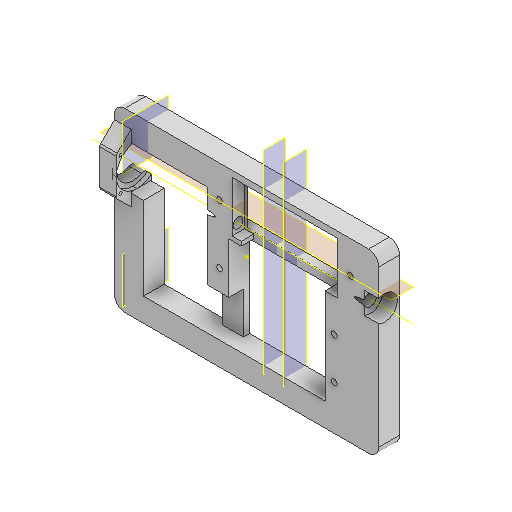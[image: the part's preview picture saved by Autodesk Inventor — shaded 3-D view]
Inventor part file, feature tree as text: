
AUTODESK INVENTOR PART (.ipt)
format: ipt  version: 2022 (Build 260153000, 153)  size: 460,800 bytes
history: native  units: mm
features: sketch x17, extrude x16, other x12, reference x8, plane x7, projected_geometry x7, fillet x3, chamfer x1, mirror x1
ambient origin geometry x8: Origin, YZ Plane, XZ Plane, XY Plane, X Axis, Y Axis, Z Axis, Center Point
bodies: Solid1 (feature_tree)
feature tree (72):
  extrude  "Extrusion1"  Depth=10.0mm
  fillet  "Fillet1"  Radius=10.0mm
  extrude  "Extrusion2"  Depth=51.0mm
  extrude  "Extrusion3"  Depth=20.0mm
  plane  "Work Plane1"
  plane  "Work Plane2"
  chamfer  "Chamfer1"  [1 undecoded]
  plane  "Work Plane3"
  extrude  "Extrusion12"  Depth=10.0mm
  extrude  "Extrusion13"  Depth=12.0mm
  mirror  "Mirror1"
  plane  "Work Plane4"
  plane  "Work Plane5"
  plane  "Arbeitsebene7"
  extrude  "Extrusion27"  Depth=7.0mm
  extrude  "Extrusion28"  Depth=0.5mm TaperAngle=0.0deg
  extrude  "Extrusion29"  Depth=0.5mm
  fillet  "Rundung6"  Radius=1.0mm
  extrude  "Extrusion37"  TaperAngle=45.0deg  [1 undecoded]
  extrude  "Extrusion38"  Depth=10.0mm
  fillet  "Rundung7"  [1 undecoded]
  extrude  "Extrusion39"  Depth=10.0mm TaperAngle=0.0deg
  other  "Arbeitsachse1"
  sketch  "Skizze44"  dims[d145=8.0mm d146=0.0mm d147=0.5mm d148=1.0mm d149=0.0mm]
  extrude  "Extrusion41"  TaperAngle=0.0deg  [1 undecoded]
  extrude  "Extrusion42"  Depth=2.0mm TaperAngle=0.0deg
  extrude  "Extrusion43"  Depth=2.5mm
  extrude  "Extrusion44"  Depth=0.5mm
  sketch  "Skizze49"  dims[d195=20.0mm d196=2.0mm d197=0.0mm d199=14.0mm d201=0.5mm d203=0.5mm d204=1.0mm d205=3.0mm d206=2.8mm d207=2.8mm d208=2.8mm d209=2.8mm d210=2.8mm d211=0.0mm d212=0.0mm d213=3.0mm d214=0.0mm d215=6.0mm d216=2.0mm d217=3.0mm d218=0.0mm d219=2.5mm d220=0.0mm]
  plane  "Arbeitsebene10"
  extrude  "Extrusion45"  Depth=0.5mm
  sketch  "Sketch1"  dims[d0=127.8mm d1=85.5mm d2=10.0mm d3=0.0mm]
  sketch  "Sketch2"  dims[d4=4.0mm d5=51.0mm]
  projected_geometry  "Projected Loop1"
  sketch  "Sketch3"  dims[d6=25.0mm d7=20.0mm]
  projected_geometry  "Projected Loop2"
  sketch  "Sketch12"  dims[d8=13.0mm]
  reference  "Reference4"
  sketch  "Sketch13"  dims[d9=6.0mm]
  sketch  "Skizze28"  dims[d10=0.0mm]
  sketch  "Skizze29"  dims[d11=1.5mm d12=0.0mm d13=0.0mm]
  reference  "Referenz13"
  sketch  "Skizze30"  dims[d14=4.0mm d15=2.0mm d16=45.0deg d38=10.0mm]
  reference  "Referenz14"
  sketch  "Skizze40"  dims[d61=30.0mm d62=-0.523599mm d63=12.0mm]
  projected_geometry  "Projizierte Kontur18"
  sketch  "Skizze41"  dims[d64=7.0mm d65=0.0mm d100=7.0mm]
  projected_geometry  "Projizierte Kontur19"
  sketch  "Skizze42"  dims[d142=0.5mm d143=40.0mm d144=0.0mm]
  reference  "Referenz22"
  reference  "Referenz23"
  reference  "Referenz24"
  reference  "Referenz25"
  sketch  "Skizze45"  dims[d150=2.0mm d151=45.0deg]
  sketch  "Skizze46"  dims[d152=45.0deg d178=10.0mm d179=0.0mm d180=0.0mm]
  projected_geometry  "Projizierte Kontur20"
  sketch  "Skizze47"  dims[d181=14.0mm d182=10.0mm d183=0.0mm]
  projected_geometry  "Projizierte Kontur21"
  sketch  "Skizze48"  dims[d184=5.0mm d187=0.0mm d188=0.0mm]
  projected_geometry  "Projizierte Kontur22"
  reference  "Referenz29"
  other  "<userpath>\Documents\GitHub\Guinardia\INVENTOR\Assembly_Guinardia_V1.iam"
  other  "Assembly_Guinardia_V1.iam"
  other  "00_PipetteTip200ul-1:2"
  other  "00_NEMA8:1"
  other  "Assembly_Guinardia_V2.iam"
  other  "Assemlby_Scanner_v1:1"
  other  "30_Scanlens_Laseradaper_v1:1"
  other  "30_Scanlens_Laseradaper_lid_v1:1"
  other  "00_Coverglass_50x24mm:2"
  other  "<userpath>\Documents\Inventor\Guinardia\INVENTOR\Assembly_Guinardia_V0.iam"
  other  "Assembly_Guinardia_V0.iam"
note: 4 required parameter values undecoded (feature->parameter linkage not recoverable at this tier; creation-order binding heuristic only, values carry confidence <= 0.55)
